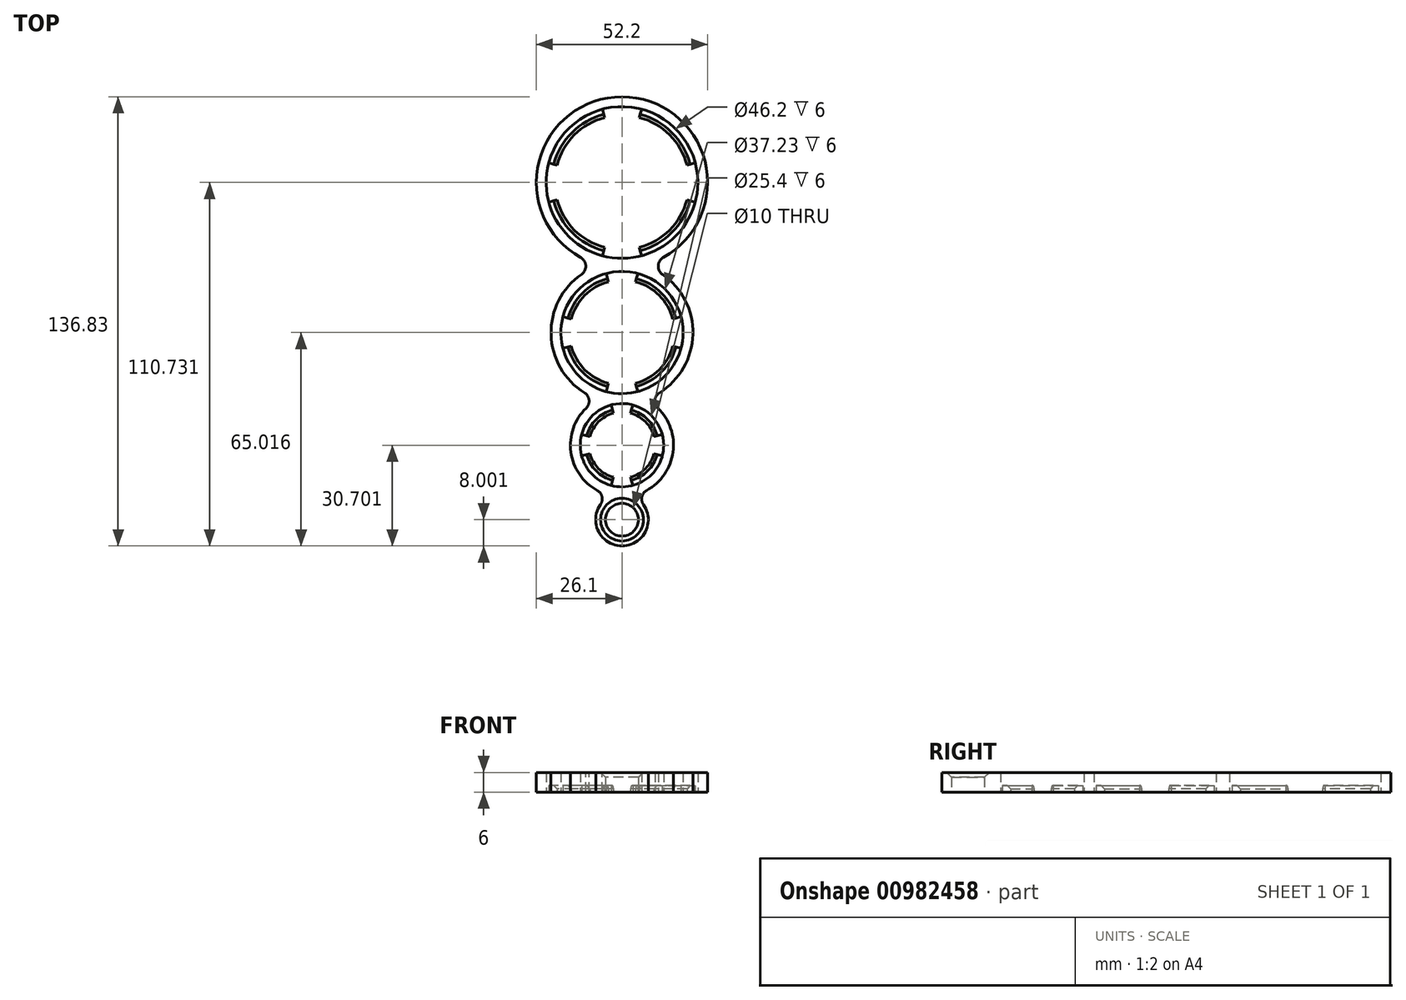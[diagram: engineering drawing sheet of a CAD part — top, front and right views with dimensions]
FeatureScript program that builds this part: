
annotation { "Feature Type Name" : "Feature", "Feature Type Description" : "" }
export const myFeature = defineFeature(function(context is Context, id is Id, definition is map)
    precondition{}
    {
        {
            var Q0;
            Q0=qCreatedBy(makeId("Top.planeOp"),FACE);
            var sketch = newSketch(context, id + "F0", { "sketchPlane" : qUnion([Q0])});
            skCircle(sketch, "E0", {"center": v(0, 234.9) * mm, "radius": 21.1 * mm, "construction": true});
            skCircle(sketch, "E1", {"center": v(0, 234.9) * mm, "radius": 16.93 * mm, "construction": true});
            skCircle(sketch, "E2", {"center": v(0, 189.19) * mm, "radius": 16.61 * mm, "construction": true});
            skCircle(sketch, "E3", {"center": v(0, 189.19) * mm, "radius": 13.01 * mm, "construction": true});
            skCircle(sketch, "E4", {"center": v(0, 154.87) * mm, "radius": 10.7 * mm, "construction": true});
            skCircle(sketch, "E5", {"center": v(0, 154.87) * mm, "radius": 7.7 * mm, "construction": true});
            skLineSegment(sketch, "E6", {"start": v(0, 0) * mm, "end": v(28.99, 281.03) * mm, "construction": true});
            skLineSegment(sketch, "E7", {"start": v(0, 0) * mm, "end": v(0, 281.73) * mm, "construction": true});
            skPoint(sketch, "E8.center", {"position": v(0, 0) * mm});
            skLineSegment(sketch, "E8.anchor1", {"start": v(0, 0) * mm, "end": v(-16, 155.17) * mm, "construction": true});
            skCircle(sketch, "E9", {"center": v(0, 234.9) * mm, "radius": 23.1 * mm});
            skCircle(sketch, "E10", {"center": v(0, 234.9) * mm, "radius": 26.1 * mm});
            skLineSegment(sketch, "E11", {"start": v(32.68, 234.9) * mm, "end": v(-37.09, 234.9) * mm, "construction": true});
            skLineSegment(sketch, "E12", {"start": v(26.96, 189.19) * mm, "end": v(-33.92, 189.19) * mm, "construction": true});
            skLineSegment(sketch, "E13", {"start": v(14.65, 154.87) * mm, "end": v(-14.4, 154.87) * mm, "construction": true});
            skCircle(sketch, "E14", {"center": v(0, 132.17) * mm, "radius": 5 * mm, "construction": true});
            skCircle(sketch, "E15", {"center": v(0, 132.17) * mm, "radius": 8 * mm, "construction": true});
            skSolve(sketch);
        }
        {
            var Q0;
            Q0 = qSketchRegion(id + "F0", true);
            extrude(context, id + "F1", {"entities" : qUnion([Q0]), "depth" : 6 * mm, "offsetDistance" : 25 * mm});
        }
        {
            var Q0;
            Q0=qCreatedBy(makeId("Top.planeOp"),FACE);
            var sketch = newSketch(context, id + "F2", { "sketchPlane" : qUnion([Q0])});
            skLineSegment(sketch, "E16", {"start": v(-5.3, 254.7) * mm, "end": v(-5.98, 257.21) * mm});
            skLineSegment(sketch, "E17", {"start": v(-19.8, 240.2) * mm, "end": v(-22.31, 240.88) * mm});
            skArc(sketch, "E18", {"start": v(-5.98, 257.21) * mm, "mid": v(-16.33, 251.24) * mm, "end": v(-22.31, 240.88) * mm});
            skArc(sketch, "E19", {"start": v(-5.3, 254.7) * mm, "mid": v(-14.5, 249.4) * mm, "end": v(-19.8, 240.2) * mm});
            skLineSegment(sketch, "E20.MirrorCS", {"start": v(19.8, 240.2) * mm, "end": v(22.31, 240.88) * mm});
            skArc(sketch, "E21.MirrorCS", {"start": v(5.3, 254.7) * mm, "mid": v(14.5, 249.4) * mm, "end": v(19.8, 240.2) * mm});
            skLineSegment(sketch, "E22.MirrorCS", {"start": v(5.3, 254.7) * mm, "end": v(5.98, 257.21) * mm});
            skArc(sketch, "E23.MirrorCS", {"start": v(5.98, 257.21) * mm, "mid": v(16.33, 251.24) * mm, "end": v(22.31, 240.88) * mm});
            skLineSegment(sketch, "E24.MirrorCS", {"start": v(19.8, 229.6) * mm, "end": v(22.31, 228.92) * mm});
            skArc(sketch, "E25.MirrorCS", {"start": v(5.3, 215.1) * mm, "mid": v(14.5, 220.4) * mm, "end": v(19.8, 229.6) * mm});
            skLineSegment(sketch, "E26.MirrorCS", {"start": v(5.3, 215.1) * mm, "end": v(5.98, 212.59) * mm});
            skArc(sketch, "E27.MirrorCS", {"start": v(5.98, 212.59) * mm, "mid": v(16.33, 218.57) * mm, "end": v(22.31, 228.92) * mm});
            skLineSegment(sketch, "E28.MirrorCS", {"start": v(-5.3, 215.1) * mm, "end": v(-5.98, 212.59) * mm});
            skArc(sketch, "E29.MirrorCS", {"start": v(-5.98, 212.59) * mm, "mid": v(-16.33, 218.57) * mm, "end": v(-22.31, 228.92) * mm});
            skArc(sketch, "E30.MirrorCS", {"start": v(-5.3, 215.1) * mm, "mid": v(-14.5, 220.4) * mm, "end": v(-19.8, 229.6) * mm});
            skLineSegment(sketch, "E31.MirrorCS", {"start": v(-19.8, 229.6) * mm, "end": v(-22.31, 228.92) * mm});
            skCircle(sketch, "E32", {"center": v(0, 132.4) * mm, "radius": 5 * mm, "construction": true});
            skCircle(sketch, "E33", {"center": v(0, 132.4) * mm, "radius": 8 * mm, "construction": true});
            skSolve(sketch);
        }
        {
            var Q0;
            Q0 = qSketchRegion(id + "F2", true);
            extrude(context, id + "F3", {"entities" : qUnion([Q0]), "operationType" : NewBodyOperationType.ADD, "depth" : 2 * mm, "offsetDistance" : 25 * mm});
        }
        {
            var Q0;
            Q0=makeQuery(id+"F3.opExtrude","CAP_EDGE",EDGE,{"disambiguationData":[OSD([sQuery(id+"F2.wireOp",EDGE,"E19")])],"isStart":false});
            var Q1;
            Q1=makeQuery(id+"F3.opExtrude","CAP_EDGE",EDGE,{"disambiguationData":[OSD([sQuery(id+"F2.wireOp",EDGE,"E21.MirrorCS")])],"isStart":false});
            var Q2;
            Q2=makeQuery(id+"F3.opExtrude","CAP_EDGE",EDGE,{"disambiguationData":[OSD([sQuery(id+"F2.wireOp",EDGE,"E25.MirrorCS")])],"isStart":false});
            var Q3;
            Q3=makeQuery(id+"F3.opExtrude","CAP_EDGE",EDGE,{"disambiguationData":[OSD([sQuery(id+"F2.wireOp",EDGE,"E30.MirrorCS")])],"isStart":false});
            chamfer(context, id + "F4", {"entities" : qUnion([Q0, Q1, Q2, Q3]), "width" : 1 * mm, "tangentPropagation" : true});
        }
        {
            var Q0;
            Q0=qCreatedBy(makeId("Top.planeOp"),FACE);
            var sketch = newSketch(context, id + "F5", { "sketchPlane" : qUnion([Q0])});
            skCircle(sketch, "E34", {"center": v(0, 189.19) * mm, "radius": 21.61 * mm});
            skCircle(sketch, "E35", {"center": v(0, 189.19) * mm, "radius": 18.61 * mm});
            skSolve(sketch);
        }
        {
            var Q0;
            Q0 = qSketchRegion(id + "F5", true);
            extrude(context, id + "F6", {"entities" : qUnion([Q0]), "operationType" : NewBodyOperationType.ADD, "depth" : 6 * mm, "offsetDistance" : 25 * mm});
        }
        {
            var Q0;
            Q0=qCreatedBy(makeId("Top.planeOp"),FACE);
            var sketch = newSketch(context, id + "F7", { "sketchPlane" : qUnion([Q0])});
            skLineSegment(sketch, "E36", {"start": v(-4.14, 204.66) * mm, "end": v(-4.82, 207.17) * mm});
            skLineSegment(sketch, "E37", {"start": v(-15.47, 193.33) * mm, "end": v(-17.98, 194) * mm});
            skArc(sketch, "E38", {"start": v(-4.14, 204.66) * mm, "mid": v(-11.32, 200.51) * mm, "end": v(-15.47, 193.33) * mm});
            skArc(sketch, "E39", {"start": v(-4.82, 207.17) * mm, "mid": v(-13.16, 202.35) * mm, "end": v(-17.98, 194) * mm});
            skLineSegment(sketch, "E40.MirrorCS", {"start": v(4.14, 204.66) * mm, "end": v(4.82, 207.17) * mm});
            skArc(sketch, "E41.MirrorCS", {"start": v(4.82, 207.17) * mm, "mid": v(13.16, 202.35) * mm, "end": v(17.98, 194) * mm});
            skArc(sketch, "E42.MirrorCS", {"start": v(4.14, 204.66) * mm, "mid": v(11.32, 200.51) * mm, "end": v(15.47, 193.33) * mm});
            skLineSegment(sketch, "E43.MirrorCS", {"start": v(15.47, 193.33) * mm, "end": v(17.98, 194) * mm});
            skLineSegment(sketch, "E44.MirrorCS", {"start": v(15.47, 185.04) * mm, "end": v(17.98, 184.37) * mm});
            skArc(sketch, "E45.MirrorCS", {"start": v(4.14, 173.72) * mm, "mid": v(11.32, 177.86) * mm, "end": v(15.47, 185.04) * mm});
            skArc(sketch, "E46.MirrorCS", {"start": v(4.82, 171.2) * mm, "mid": v(13.16, 176.02) * mm, "end": v(17.98, 184.37) * mm});
            skLineSegment(sketch, "E47.MirrorCS", {"start": v(4.14, 173.72) * mm, "end": v(4.82, 171.2) * mm});
            skLineSegment(sketch, "E48.MirrorCS", {"start": v(-4.14, 173.72) * mm, "end": v(-4.82, 171.2) * mm});
            skArc(sketch, "E49.MirrorCS", {"start": v(-4.82, 171.2) * mm, "mid": v(-13.16, 176.02) * mm, "end": v(-17.98, 184.37) * mm});
            skArc(sketch, "E50.MirrorCS", {"start": v(-4.14, 173.72) * mm, "mid": v(-11.32, 177.86) * mm, "end": v(-15.47, 185.04) * mm});
            skLineSegment(sketch, "E51.MirrorCS", {"start": v(-15.47, 185.04) * mm, "end": v(-17.98, 184.37) * mm});
            skSolve(sketch);
        }
        {
            var Q0;
            Q0 = qSketchRegion(id + "F7", true);
            extrude(context, id + "F8", {"entities" : qUnion([Q0]), "operationType" : NewBodyOperationType.ADD, "depth" : 2 * mm, "offsetDistance" : 25 * mm});
        }
        {
            var Q0;
            Q0=makeQuery(id+"F8.opExtrude","CAP_EDGE",EDGE,{"disambiguationData":[OSD([sQuery(id+"F7.wireOp",EDGE,"E38")])],"isStart":false});
            var Q1;
            Q1=makeQuery(id+"F8.opExtrude","CAP_EDGE",EDGE,{"disambiguationData":[OSD([sQuery(id+"F7.wireOp",EDGE,"E42.MirrorCS")])],"isStart":false});
            var Q2;
            Q2=makeQuery(id+"F8.opExtrude","CAP_EDGE",EDGE,{"disambiguationData":[OSD([sQuery(id+"F7.wireOp",EDGE,"E45.MirrorCS")])],"isStart":false});
            var Q3;
            Q3=makeQuery(id+"F8.opExtrude","CAP_EDGE",EDGE,{"disambiguationData":[OSD([sQuery(id+"F7.wireOp",EDGE,"E50.MirrorCS")])],"isStart":false});
            chamfer(context, id + "F9", {"entities" : qUnion([Q0, Q1, Q2, Q3]), "width" : 1 * mm, "tangentPropagation" : true});
        }
        {
            var Q0;
            Q0=qCreatedBy(makeId("Top.planeOp"),FACE);
            var sketch = newSketch(context, id + "F10", { "sketchPlane" : qUnion([Q0])});
            skCircle(sketch, "E52", {"center": v(0, 154.87) * mm, "radius": 15.7 * mm});
            skCircle(sketch, "E53", {"center": v(0, 154.87) * mm, "radius": 12.7 * mm});
            skSolve(sketch);
        }
        {
            var Q0;
            Q0 = qSketchRegion(id + "F10", true);
            extrude(context, id + "F11", {"entities" : qUnion([Q0]), "operationType" : NewBodyOperationType.ADD, "depth" : 6 * mm, "offsetDistance" : 25 * mm});
        }
        {
            var Q0;
            Q0=qCreatedBy(makeId("Top.planeOp"),FACE);
            var sketch = newSketch(context, id + "F12", { "sketchPlane" : qUnion([Q0])});
            skArc(sketch, "E54", {"start": v(-3.29, 167.14) * mm, "mid": v(-8.98, 163.85) * mm, "end": v(-12.27, 158.16) * mm});
            skArc(sketch, "E55", {"start": v(-2.61, 164.63) * mm, "mid": v(-7.14, 162.01) * mm, "end": v(-9.76, 157.49) * mm});
            skLineSegment(sketch, "E56", {"start": v(-2.61, 164.63) * mm, "end": v(-3.29, 167.14) * mm});
            skLineSegment(sketch, "E57", {"start": v(-9.76, 157.49) * mm, "end": v(-12.27, 158.16) * mm});
            skLineSegment(sketch, "E58.MirrorCS", {"start": v(2.61, 164.63) * mm, "end": v(3.29, 167.14) * mm});
            skArc(sketch, "E59.MirrorCS", {"start": v(3.29, 167.14) * mm, "mid": v(8.98, 163.85) * mm, "end": v(12.27, 158.16) * mm});
            skArc(sketch, "E60.MirrorCS", {"start": v(2.61, 164.63) * mm, "mid": v(7.14, 162.01) * mm, "end": v(9.76, 157.49) * mm});
            skLineSegment(sketch, "E61.MirrorCS", {"start": v(9.76, 157.49) * mm, "end": v(12.27, 158.16) * mm});
            skLineSegment(sketch, "E62.MirrorCS", {"start": v(9.76, 152.26) * mm, "end": v(12.27, 151.58) * mm});
            skArc(sketch, "E63.MirrorCS", {"start": v(2.61, 145.12) * mm, "mid": v(7.14, 147.73) * mm, "end": v(9.76, 152.26) * mm});
            skArc(sketch, "E64.MirrorCS", {"start": v(3.29, 142.6) * mm, "mid": v(8.98, 145.9) * mm, "end": v(12.27, 151.58) * mm});
            skLineSegment(sketch, "E65.MirrorCS", {"start": v(2.61, 145.12) * mm, "end": v(3.29, 142.6) * mm});
            skLineSegment(sketch, "E66.MirrorCS", {"start": v(-2.61, 145.12) * mm, "end": v(-3.29, 142.6) * mm});
            skArc(sketch, "E67.MirrorCS", {"start": v(-2.61, 145.12) * mm, "mid": v(-7.14, 147.73) * mm, "end": v(-9.76, 152.26) * mm});
            skLineSegment(sketch, "E68.MirrorCS", {"start": v(-9.76, 152.26) * mm, "end": v(-12.27, 151.58) * mm});
            skArc(sketch, "E69.MirrorCS", {"start": v(-3.29, 142.6) * mm, "mid": v(-8.98, 145.9) * mm, "end": v(-12.27, 151.58) * mm});
            skSolve(sketch);
        }
        {
            var Q0;
            Q0 = qSketchRegion(id + "F12", true);
            extrude(context, id + "F13", {"entities" : qUnion([Q0]), "operationType" : NewBodyOperationType.ADD, "depth" : 2 * mm, "offsetDistance" : 25 * mm});
        }
        {
            var Q0;
            Q0=makeQuery(id+"F13.opExtrude","CAP_EDGE",EDGE,{"disambiguationData":[OSD([sQuery(id+"F12.wireOp",EDGE,"E55")])],"isStart":false});
            var Q1;
            Q1=makeQuery(id+"F13.opExtrude","CAP_EDGE",EDGE,{"disambiguationData":[OSD([sQuery(id+"F12.wireOp",EDGE,"E60.MirrorCS")])],"isStart":false});
            var Q2;
            Q2=makeQuery(id+"F13.opExtrude","CAP_EDGE",EDGE,{"disambiguationData":[OSD([sQuery(id+"F12.wireOp",EDGE,"E63.MirrorCS")])],"isStart":false});
            var Q3;
            Q3=makeQuery(id+"F13.opExtrude","CAP_EDGE",EDGE,{"disambiguationData":[OSD([sQuery(id+"F12.wireOp",EDGE,"E67.MirrorCS")])],"isStart":false});
            chamfer(context, id + "F14", {"entities" : qUnion([Q0, Q1, Q2, Q3]), "width" : 1 * mm, "tangentPropagation" : true});
        }
        {
            var Q0;
            Q0=qCreatedBy(makeId("Top.planeOp"),FACE);
            var sketch = newSketch(context, id + "F15", { "sketchPlane" : qUnion([Q0])});
            skCircle(sketch, "E70", {"center": v(0, 132.17) * mm, "radius": 5 * mm});
            skCircle(sketch, "E71", {"center": v(0, 132.17) * mm, "radius": 8 * mm});
            skSolve(sketch);
        }
        {
            var Q0;
            Q0 = qSketchRegion(id + "F15", true);
            extrude(context, id + "F16", {"entities" : qUnion([Q0]), "operationType" : NewBodyOperationType.ADD, "depth" : 6 * mm, "offsetDistance" : 25 * mm});
        }
        {
            var Q0;
            Q0=makeQuery(id+"F16.opExtrude","CAP_EDGE",EDGE,{"disambiguationData":[OSD([sQuery(id+"F15.wireOp",EDGE,"E70")])],"isStart":false});
            chamfer(context, id + "F17", {"entities" : qUnion([Q0]), "width" : 1.5 * mm, "tangentPropagation" : true});
        }
        {
            var Q0;
            Q0=makeQuery(id+"F6.boolean.opBoolean","INTERSECT",EDGE,{"disambiguationData":[OD(0.0)],"derivedFrom":[makeQuery(id+"F1.opExtrude","SWEPT_FACE",FACE,{"disambiguationData":[OSD([sQuery(id+"F0.wireOp",EDGE,"E10")])]}),makeQuery(id+"F6.opExtrude","SWEPT_FACE",FACE,{"disambiguationData":[OSD([sQuery(id+"F5.wireOp",EDGE,"E34")])]})]});
            var Q1;
            Q1=makeQuery(id+"F6.boolean.opBoolean","INTERSECT",EDGE,{"disambiguationData":[OD(1.0)],"derivedFrom":[makeQuery(id+"F1.opExtrude","SWEPT_FACE",FACE,{"disambiguationData":[OSD([sQuery(id+"F0.wireOp",EDGE,"E10")])]}),makeQuery(id+"F6.opExtrude","SWEPT_FACE",FACE,{"disambiguationData":[OSD([sQuery(id+"F5.wireOp",EDGE,"E34")])]})]});
            var Q2;
            Q2=makeQuery(id+"F11.boolean.opBoolean","INTERSECT",EDGE,{"disambiguationData":[OD(1.0)],"derivedFrom":[makeQuery(id+"F6.opExtrude","SWEPT_FACE",FACE,{"disambiguationData":[OSD([sQuery(id+"F5.wireOp",EDGE,"E34")])]}),makeQuery(id+"F11.opExtrude","SWEPT_FACE",FACE,{"disambiguationData":[OSD([sQuery(id+"F10.wireOp",EDGE,"E52")])]})]});
            var Q3;
            Q3=makeQuery(id+"F11.boolean.opBoolean","INTERSECT",EDGE,{"disambiguationData":[OD(0.0)],"derivedFrom":[makeQuery(id+"F6.opExtrude","SWEPT_FACE",FACE,{"disambiguationData":[OSD([sQuery(id+"F5.wireOp",EDGE,"E34")])]}),makeQuery(id+"F11.opExtrude","SWEPT_FACE",FACE,{"disambiguationData":[OSD([sQuery(id+"F10.wireOp",EDGE,"E52")])]})]});
            var Q4;
            Q4=makeQuery(id+"F16.boolean.opBoolean","INTERSECT",EDGE,{"disambiguationData":[OD(0.0)],"derivedFrom":[makeQuery(id+"F11.opExtrude","SWEPT_FACE",FACE,{"disambiguationData":[OSD([sQuery(id+"F10.wireOp",EDGE,"E52")])]}),makeQuery(id+"F16.opExtrude","SWEPT_FACE",FACE,{"disambiguationData":[OSD([sQuery(id+"F15.wireOp",EDGE,"E71")])]})]});
            var Q5;
            Q5=makeQuery(id+"F16.boolean.opBoolean","INTERSECT",EDGE,{"disambiguationData":[OD(1.0)],"derivedFrom":[makeQuery(id+"F11.opExtrude","SWEPT_FACE",FACE,{"disambiguationData":[OSD([sQuery(id+"F10.wireOp",EDGE,"E52")])]}),makeQuery(id+"F16.opExtrude","SWEPT_FACE",FACE,{"disambiguationData":[OSD([sQuery(id+"F15.wireOp",EDGE,"E71")])]})]});
            fillet(context, id + "F18", {"entities" : qUnion([Q0, Q1, Q2, Q3, Q4, Q5]), "radius" : 3 * mm, "tangentPropagation" : true, "allowEdgeOverflow" : false});
        }
    });
